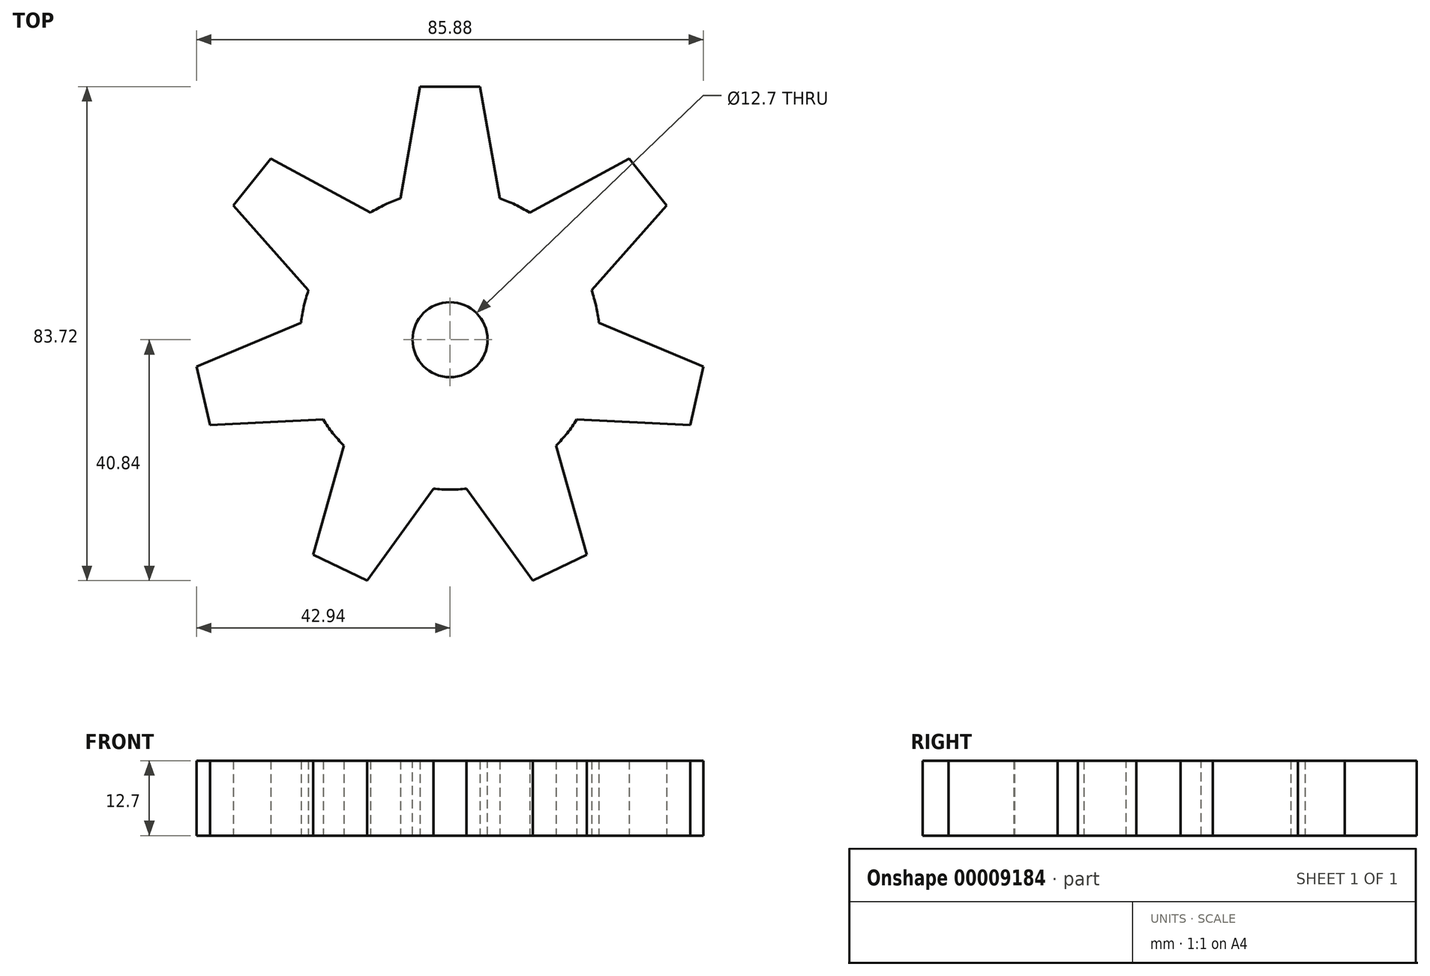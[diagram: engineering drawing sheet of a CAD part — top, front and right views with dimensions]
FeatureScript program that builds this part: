
annotation { "Feature Type Name" : "Feature", "Feature Type Description" : "" }
export const myFeature = defineFeature(function(context is Context, id is Id, definition is map)
    precondition{}
    {
        {
            var Q0;
            Q0=qCreatedBy(makeId("Top.planeOp"),FACE);
            var sketch = newSketch(context, id + "F0", { "sketchPlane" : qUnion([Q0])});
            skCircle(sketch, "E0", {"center": v(0, 0) * mm, "radius": 25.4 * mm});
            skLineSegment(sketch, "E1", {"start": v(0, 0) * mm, "end": v(0, 25.4) * mm, "construction": true});
            skLineSegment(sketch, "E2", {"start": v(-8.42, 23.97) * mm, "end": v(-5.08, 42.88) * mm});
            skLineSegment(sketch, "E3", {"start": v(-5.08, 42.88) * mm, "end": v(0, 42.88) * mm});
            skLineSegment(sketch, "E4.MirrorCS", {"start": v(8.42, 23.97) * mm, "end": v(5.08, 42.88) * mm});
            skLineSegment(sketch, "E5.MirrorCS", {"start": v(5.08, 42.88) * mm, "end": v(0, 42.88) * mm});
            skLineSegment(sketch, "E6.1.0", {"start": v(-23.98, 8.36) * mm, "end": v(-36.7, 22.76) * mm});
            skLineSegment(sketch, "E6.1.1", {"start": v(-36.7, 22.76) * mm, "end": v(-33.53, 26.74) * mm});
            skLineSegment(sketch, "E6.1.2", {"start": v(-30.36, 30.7) * mm, "end": v(-33.53, 26.74) * mm});
            skLineSegment(sketch, "E6.1.3", {"start": v(-13.5, 21.52) * mm, "end": v(-30.36, 30.7) * mm});
            skLineSegment(sketch, "E6.2.0", {"start": v(-21.5, -13.54) * mm, "end": v(-40.67, -14.5) * mm});
            skLineSegment(sketch, "E6.2.1", {"start": v(-40.67, -14.5) * mm, "end": v(-41.8, -9.54) * mm});
            skLineSegment(sketch, "E6.2.2", {"start": v(-42.94, -4.59) * mm, "end": v(-41.8, -9.54) * mm});
            skLineSegment(sketch, "E6.2.3", {"start": v(-25.24, 2.87) * mm, "end": v(-42.94, -4.59) * mm});
            skLineSegment(sketch, "E6.3.0", {"start": v(-2.82, -25.24) * mm, "end": v(-14.03, -40.84) * mm});
            skLineSegment(sketch, "E6.3.1", {"start": v(-14.03, -40.84) * mm, "end": v(-18.6, -38.63) * mm});
            skLineSegment(sketch, "E6.3.2", {"start": v(-23.18, -36.43) * mm, "end": v(-18.6, -38.63) * mm});
            skLineSegment(sketch, "E6.3.3", {"start": v(-17.98, -17.94) * mm, "end": v(-23.18, -36.43) * mm});
            skLineSegment(sketch, "E6.4.0", {"start": v(17.98, -17.94) * mm, "end": v(23.18, -36.43) * mm});
            skLineSegment(sketch, "E6.4.1", {"start": v(23.18, -36.43) * mm, "end": v(18.6, -38.63) * mm});
            skLineSegment(sketch, "E6.4.2", {"start": v(14.03, -40.84) * mm, "end": v(18.6, -38.63) * mm});
            skLineSegment(sketch, "E6.4.3", {"start": v(2.82, -25.24) * mm, "end": v(14.03, -40.84) * mm});
            skLineSegment(sketch, "E7.1.5.0", {"start": v(25.24, 2.87) * mm, "end": v(42.94, -4.59) * mm});
            skLineSegment(sketch, "E7.3.5.0", {"start": v(42.94, -4.59) * mm, "end": v(41.8, -9.54) * mm});
            skLineSegment(sketch, "E7.6.5.0", {"start": v(40.67, -14.5) * mm, "end": v(41.8, -9.54) * mm});
            skLineSegment(sketch, "E7.9.5.0", {"start": v(21.5, -13.54) * mm, "end": v(40.67, -14.5) * mm});
            skLineSegment(sketch, "E7.1.6.0", {"start": v(13.5, 21.52) * mm, "end": v(30.36, 30.7) * mm});
            skLineSegment(sketch, "E7.3.6.0", {"start": v(30.36, 30.7) * mm, "end": v(33.53, 26.74) * mm});
            skLineSegment(sketch, "E7.6.6.0", {"start": v(36.7, 22.76) * mm, "end": v(33.53, 26.74) * mm});
            skLineSegment(sketch, "E7.9.6.0", {"start": v(23.98, 8.36) * mm, "end": v(36.7, 22.76) * mm});
            skSolve(sketch);
        }
        {
            var Q0;
            {var subQ0=sQuery(id+"F0.wireOp",EDGE,"E0");var subQ10=makeQuery(id+"F0.imprint","INTERSECT",VERTEX,{"derivedFrom":[subQ0,sQuery(id+"F0.wireOp",EDGE,"E4.MirrorCS")]});Q0=makeQuery(id+"F0.imprint","IMPRINT",FACE,{"disambiguationData":[TD([[makeQuery(id+"F0.imprint","IMPRINT",EDGE,{"disambiguationData":[TD([[subQ10,1.0]])],"derivedFrom":subQ0}),1.0]])]});}
            var Q1;
            {var subQ1=sQuery(id+"F0.wireOp",EDGE,"E6.2.0");Q1=makeQuery(id+"F0.imprint","IMPRINT",FACE,{"disambiguationData":[TD([[makeQuery(id+"F0.imprint","IMPRINT",EDGE,{"derivedFrom":subQ1}),-1.0]])]});}
            var Q2;
            {var subQ1=sQuery(id+"F0.wireOp",EDGE,"E6.3.0");Q2=makeQuery(id+"F0.imprint","IMPRINT",FACE,{"disambiguationData":[TD([[makeQuery(id+"F0.imprint","IMPRINT",EDGE,{"derivedFrom":subQ1}),-1.0]])]});}
            var Q3;
            {var subQ1=sQuery(id+"F0.wireOp",EDGE,"E6.1.0");Q3=makeQuery(id+"F0.imprint","IMPRINT",FACE,{"disambiguationData":[TD([[makeQuery(id+"F0.imprint","IMPRINT",EDGE,{"derivedFrom":subQ1}),-1.0]])]});}
            var Q4;
            {var subQ1=sQuery(id+"F0.wireOp",EDGE,"E2");Q4=makeQuery(id+"F0.imprint","IMPRINT",FACE,{"disambiguationData":[TD([[makeQuery(id+"F0.imprint","IMPRINT",EDGE,{"derivedFrom":subQ1}),-1.0]])]});}
            var Q5;
            {var subQ1=sQuery(id+"F0.wireOp",EDGE,"E6.4.0");Q5=makeQuery(id+"F0.imprint","IMPRINT",FACE,{"disambiguationData":[TD([[makeQuery(id+"F0.imprint","IMPRINT",EDGE,{"derivedFrom":subQ1}),-1.0]])]});}
            var Q6;
            {var subQ1=sQuery(id+"F0.wireOp",EDGE,"E7.1.6.0");Q6=makeQuery(id+"F0.imprint","IMPRINT",FACE,{"disambiguationData":[TD([[makeQuery(id+"F0.imprint","IMPRINT",EDGE,{"derivedFrom":subQ1}),-1.0]])]});}
            var Q7;
            {var subQ1=sQuery(id+"F0.wireOp",EDGE,"E7.1.5.0");Q7=makeQuery(id+"F0.imprint","IMPRINT",FACE,{"disambiguationData":[TD([[makeQuery(id+"F0.imprint","IMPRINT",EDGE,{"derivedFrom":subQ1}),-1.0]])]});}
            extrude(context, id + "F1", {"entities" : qUnion([Q0, Q1, Q2, Q3, Q4, Q5, Q6, Q7]), "depth" : 12.7 * mm});
        }
        {
            var Q0;
            Q0=makeQuery(id+"F1.opExtrude","CAP_FACE",FACE,{"disambiguationData":[OSD([sQuery(id+"F0.wireOp",EDGE,"E0"),sQuery(id+"F0.wireOp",EDGE,"E2"),sQuery(id+"F0.wireOp",EDGE,"E3"),sQuery(id+"F0.wireOp",EDGE,"E4.MirrorCS"),sQuery(id+"F0.wireOp",EDGE,"E5.MirrorCS"),sQuery(id+"F0.wireOp",EDGE,"E6.1.0"),sQuery(id+"F0.wireOp",EDGE,"E6.1.1"),sQuery(id+"F0.wireOp",EDGE,"E6.1.2"),sQuery(id+"F0.wireOp",EDGE,"E6.1.3"),sQuery(id+"F0.wireOp",EDGE,"E6.2.0"),sQuery(id+"F0.wireOp",EDGE,"E6.2.1"),sQuery(id+"F0.wireOp",EDGE,"E6.2.2"),sQuery(id+"F0.wireOp",EDGE,"E6.2.3"),sQuery(id+"F0.wireOp",EDGE,"E6.3.0"),sQuery(id+"F0.wireOp",EDGE,"E6.3.1"),sQuery(id+"F0.wireOp",EDGE,"E6.3.2"),sQuery(id+"F0.wireOp",EDGE,"E6.3.3"),sQuery(id+"F0.wireOp",EDGE,"E6.4.0"),sQuery(id+"F0.wireOp",EDGE,"E6.4.1"),sQuery(id+"F0.wireOp",EDGE,"E6.4.2"),sQuery(id+"F0.wireOp",EDGE,"E6.4.3")])],"isStart":false});
            var sketch = newSketch(context, id + "F2", { "sketchPlane" : qUnion([Q0])});
            skCircle(sketch, "E8", {"center": v(0, 0) * mm, "radius": 6.35 * mm});
            skSolve(sketch);
        }
        {
            var Q0;
            Q0 = qSketchRegion(id + "F2", true);
            extrude(context, id + "F3", {"entities" : qUnion([Q0]), "operationType" : NewBodyOperationType.REMOVE, "endBound" : BoundingType.THROUGH_ALL, "oppositeDirection" : true, "depth" : 25.4 * mm});
        }
    });
